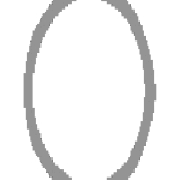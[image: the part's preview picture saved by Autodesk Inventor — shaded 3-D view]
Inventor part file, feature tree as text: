
AUTODESK INVENTOR PART (.ipt)
format: ipt  version: 2021 (Build 250183000, 183)  size: 109,568 bytes
history: native  units: in
note: dims shown in document units (in); Inventor stores cm internally (conversion verified against a paired STEP export)
features: other x4, sketch x3, plane x1
ambient origin geometry x8: Origin, YZ Plane, XZ Plane, XY Plane, X Axis, Y Axis, Z Axis, Center Point
bodies: Solid1 (feature_tree), Body (feature_tree)
feature tree (8):
  other  "Driven Length"
  other  "Frame Generator"
  other  "Start Plane"
  other  "End Plane"
  sketch  "Sketch"  dims[d2=13.5957in d4=-0.0in d5=13.5957in d6=0.12in d7=0.0in d8=90.0deg d9=13.5957in]
  sketch  "Sketch2"  dims[d0=1.0in]
  plane  "Work Plane3"
  sketch  "Sketch3"  dims[d1=0.065in]
